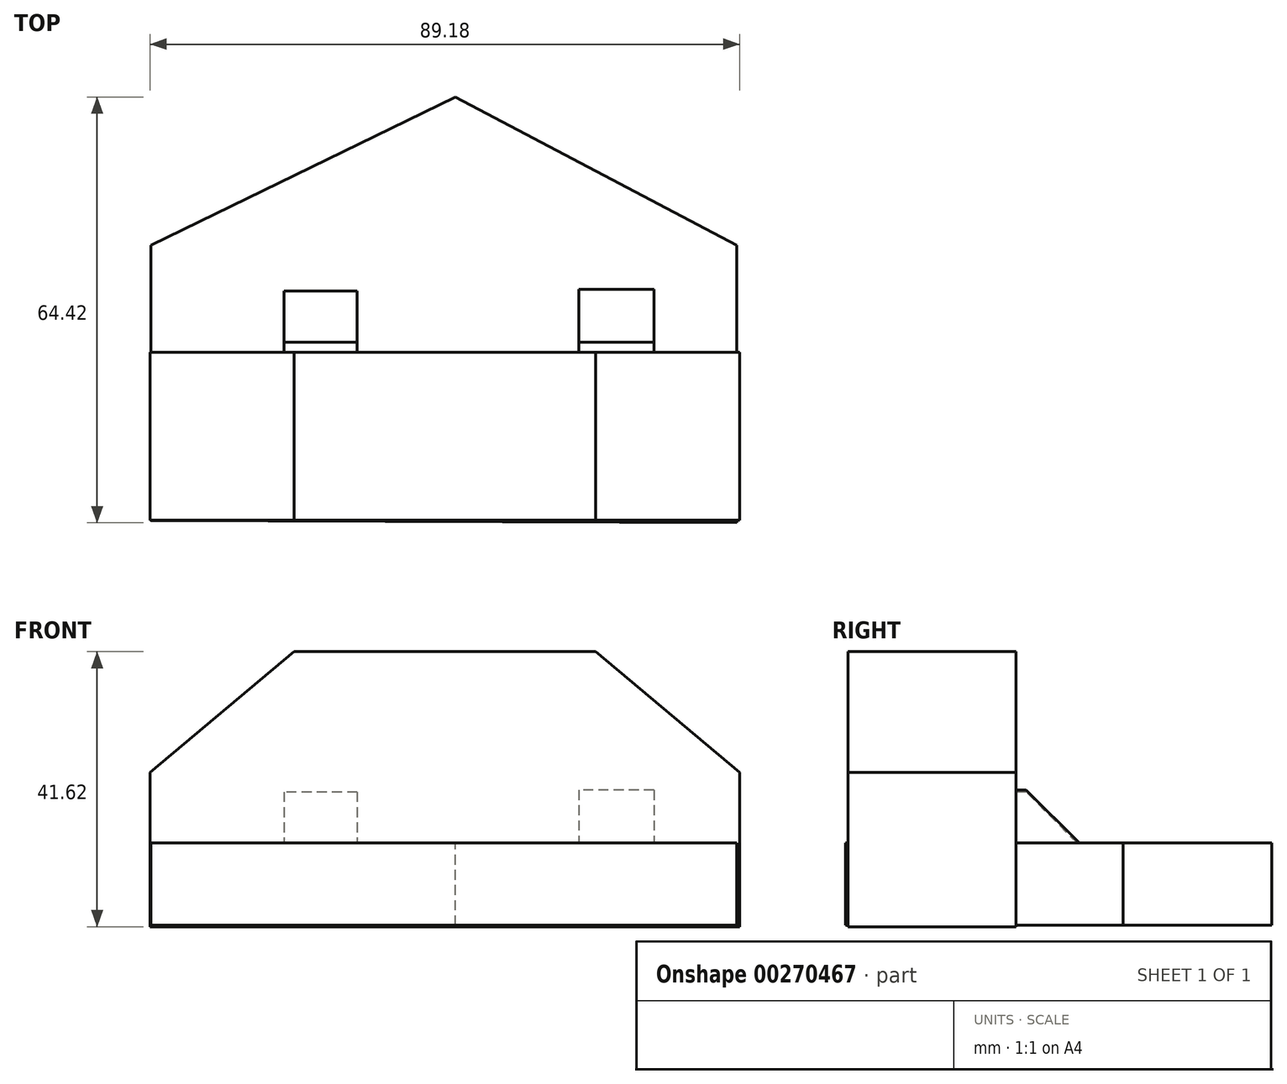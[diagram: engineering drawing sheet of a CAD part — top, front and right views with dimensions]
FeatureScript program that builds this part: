
annotation { "Feature Type Name" : "Feature", "Feature Type Description" : "" }
export const myFeature = defineFeature(function(context is Context, id is Id, definition is map)
    precondition{}
    {
        {
            var Q0;
            Q0=qCreatedBy(makeId("Front.planeOp"),FACE);
            var sketch = newSketch(context, id + "F0", { "sketchPlane" : qUnion([Q0])});
            skLineSegment(sketch, "E0", {"start": v(-56.98, -12.65) * mm, "end": v(32.2, -12.65) * mm});
            skLineSegment(sketch, "E1", {"start": v(32.2, -12.65) * mm, "end": v(32.2, 10.7) * mm});
            skLineSegment(sketch, "E2", {"start": v(-56.98, -12.65) * mm, "end": v(-56.98, 10.7) * mm});
            skLineSegment(sketch, "E3", {"start": v(-56.98, 10.7) * mm, "end": v(-35.18, 28.97) * mm});
            skLineSegment(sketch, "E4", {"start": v(-35.18, 28.97) * mm, "end": v(10.4, 28.97) * mm});
            skLineSegment(sketch, "E5", {"start": v(10.4, 28.97) * mm, "end": v(32.2, 10.7) * mm});
            skSolve(sketch);
        }
        {
            var Q0;
            Q0=makeQuery(id+"F0.imprint","IMPRINT",FACE,{"disambiguationData":[TD([[makeQuery(id+"F0.imprint","IMPRINT",EDGE,{"derivedFrom":sQuery(id+"F0.wireOp",EDGE,"E0")}),1.0]])]});
            extrude(context, id + "F1", {"entities" : qUnion([Q0]), "depth" : 25.4 * mm});
        }
        {
            var Q0;
            Q0=qCreatedBy(makeId("Top.planeOp"),FACE);
            var sketch = newSketch(context, id + "F2", { "sketchPlane" : qUnion([Q0])});
            skLineSegment(sketch, "E6", {"start": v(-56.84, -25.5) * mm, "end": v(-56.84, 16.18) * mm});
            skLineSegment(sketch, "E7", {"start": v(31.77, -25.8) * mm, "end": v(31.77, 16.18) * mm});
            skLineSegment(sketch, "E8", {"start": v(31.77, 0) * mm, "end": v(-56.84, 0) * mm});
            skLineSegment(sketch, "E9", {"start": v(-56.84, 0) * mm, "end": v(-56.84, -25.5) * mm});
            skLineSegment(sketch, "E10", {"start": v(31.77, -25.8) * mm, "end": v(-56.84, -25.5) * mm});
            skLineSegment(sketch, "E11", {"start": v(-56.84, 16.18) * mm, "end": v(-10.78, 38.62) * mm});
            skLineSegment(sketch, "E12", {"start": v(-10.78, 38.62) * mm, "end": v(31.77, 16.18) * mm});
            skSolve(sketch);
        }
        {
            var Q0;
            Q0 = qSketchRegion(id + "F2", true);
            extrude(context, id + "F3", {"entities" : qUnion([Q0]), "operationType" : NewBodyOperationType.ADD, "oppositeDirection" : true, "depth" : 12.45 * mm});
        }
        {
            var Q0;
            Q0=qCreatedBy(makeId("Front.planeOp"),FACE);
            var sketch = newSketch(context, id + "F4", { "sketchPlane" : qUnion([Q0])});
            skLineSegment(sketch, "E13.bottom", {"start": v(19.24, 8.02) * mm, "end": v(7.87, 8.02) * mm});
            skLineSegment(sketch, "E13.top", {"start": v(19.24, 0) * mm, "end": v(7.87, 0) * mm});
            skLineSegment(sketch, "E13.left", {"start": v(19.24, 8.02) * mm, "end": v(19.24, 0) * mm});
            skLineSegment(sketch, "E13.right", {"start": v(7.87, 8.02) * mm, "end": v(7.87, 0) * mm});
            skLineSegment(sketch, "E14.bottom", {"start": v(-25.65, 7.72) * mm, "end": v(-36.73, 7.72) * mm});
            skLineSegment(sketch, "E14.top", {"start": v(-25.65, 0) * mm, "end": v(-36.73, 0) * mm});
            skLineSegment(sketch, "E14.left", {"start": v(-25.65, 7.72) * mm, "end": v(-25.65, 0) * mm});
            skLineSegment(sketch, "E14.right", {"start": v(-36.73, 7.72) * mm, "end": v(-36.73, 0) * mm});
            skSolve(sketch);
        }
        {
            var Q0;
            Q0 = qSketchRegion(id + "F4", true);
            extrude(context, id + "F5", {"entities" : qUnion([Q0]), "operationType" : NewBodyOperationType.ADD, "oppositeDirection" : true, "depth" : 14.22 * mm});
        }
        {
            var Q0;
            Q0=makeQuery(id+"F5.opExtrude","CAP_EDGE",EDGE,{"disambiguationData":[OSD([sQuery(id+"F4.wireOp",EDGE,"E13.bottom")])],"isStart":false});
            chamfer(context, id + "F6", {"entities" : qUnion([Q0]), "width" : 12.7 * mm, "tangentPropagation" : true});
        }
        {
            var Q0;
            Q0=makeQuery(id+"F5.opExtrude","CAP_EDGE",EDGE,{"disambiguationData":[OSD([sQuery(id+"F4.wireOp",EDGE,"E14.bottom")])],"isStart":false});
            chamfer(context, id + "F7", {"entities" : qUnion([Q0]), "width" : 12.7 * mm, "tangentPropagation" : true});
        }
    });
